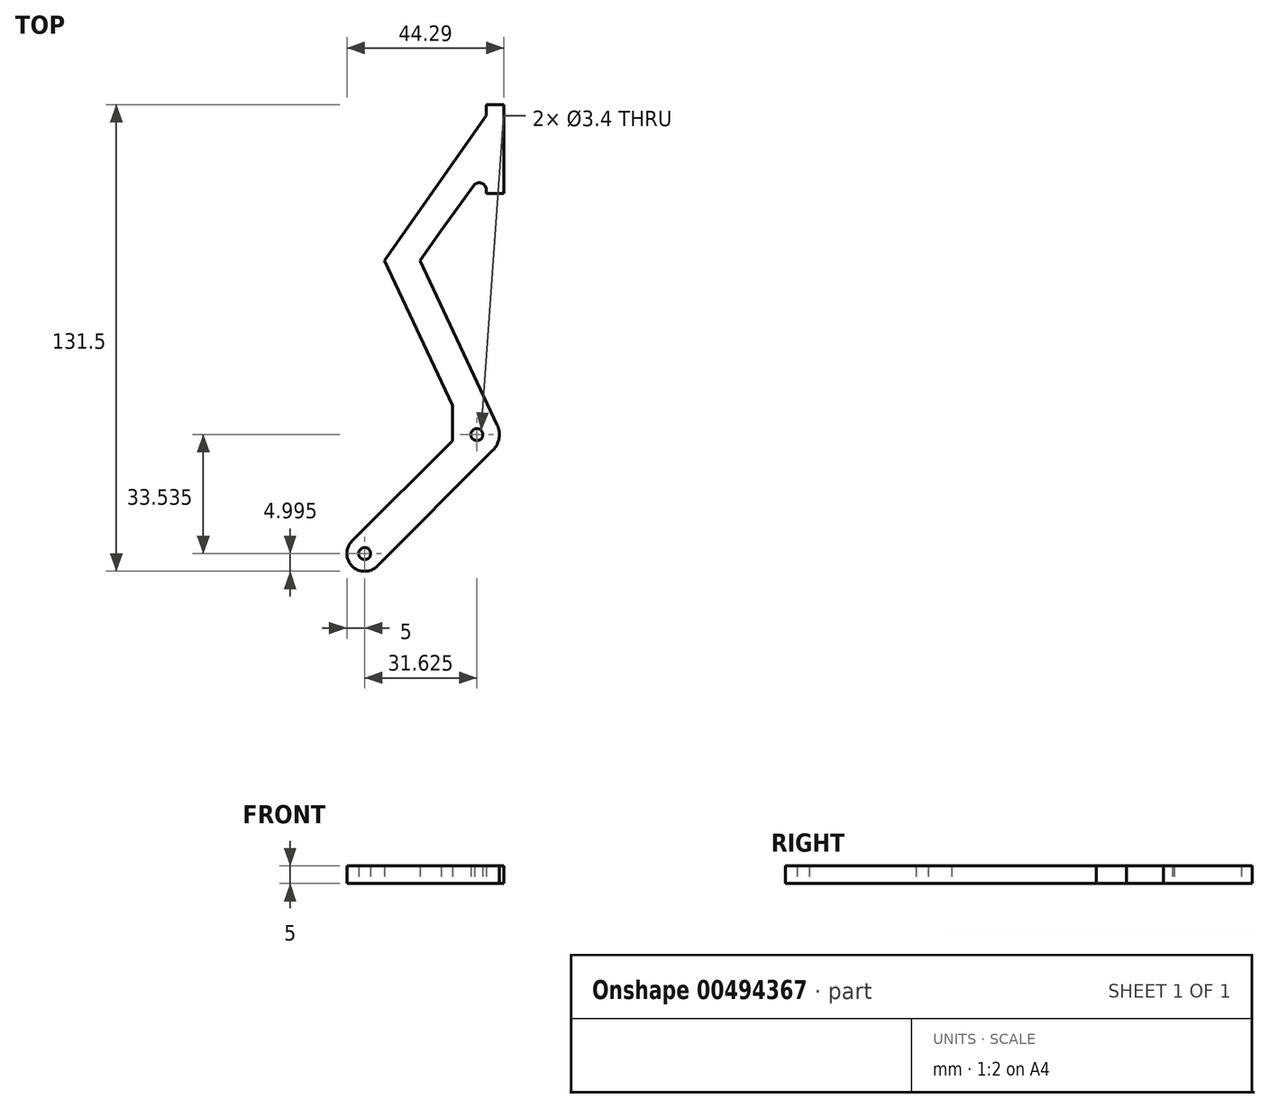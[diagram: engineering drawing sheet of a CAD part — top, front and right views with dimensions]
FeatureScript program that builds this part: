
annotation { "Feature Type Name" : "Feature", "Feature Type Description" : "" }
export const myFeature = defineFeature(function(context is Context, id is Id, definition is map)
    precondition{}
    {
        {
            var Q0;
            Q0=qCreatedBy(makeId("Top.planeOp"),FACE);
            var sketch = newSketch(context, id + "F0", { "sketchPlane" : qUnion([Q0])});
            skLineSegment(sketch, "E0", {"start": v(28.64, 109.53) * mm, "end": v(33.64, 109.53) * mm});
            skLineSegment(sketch, "E1", {"start": v(33.64, 109.53) * mm, "end": v(33.64, 84.53) * mm});
            skLineSegment(sketch, "E2", {"start": v(33.64, 84.53) * mm, "end": v(28.64, 84.53) * mm});
            skLineSegment(sketch, "E3", {"start": v(28.64, 109.53) * mm, "end": v(28.64, 106.53) * mm});
            skLineSegment(sketch, "E4", {"start": v(28.64, 84.53) * mm, "end": v(28.64, 85.53) * mm});
            skLineSegment(sketch, "E5", {"start": v(28.64, 106.53) * mm, "end": v(-0.04, 65.57) * mm});
            skLineSegment(sketch, "E6", {"start": v(-0.04, 65.57) * mm, "end": v(19.1, 24.85) * mm});
            skLineSegment(sketch, "E7", {"start": v(9.96, 65.57) * mm, "end": v(31.72, 19.26) * mm});
            skLineSegment(sketch, "E8", {"start": v(19.1, 24.85) * mm, "end": v(19.1, 14.85) * mm});
            skLineSegment(sketch, "E9", {"start": v(19.1, 14.85) * mm, "end": v(-9.19, -13.44) * mm});
            skLineSegment(sketch, "E10", {"start": v(9.96, 65.57) * mm, "end": v(15.97, 74.15) * mm});
            skArc(sketch, "E11", {"start": v(28.64, 85.53) * mm, "mid": v(27.47, 87.35) * mm, "end": v(25.33, 87.04) * mm});
            skLineSegment(sketch, "E12", {"start": v(15.97, 74.15) * mm, "end": v(25.33, 87.04) * mm});
            skLineSegment(sketch, "E13", {"start": v(19.1, 14.85) * mm, "end": v(26.17, 7.77) * mm});
            skLineSegment(sketch, "E14", {"start": v(26.17, 7.77) * mm, "end": v(30.47, 12.07) * mm});
            skPoint(sketch, "E15.newPointA", {"position": v(35.48, 11.27) * mm});
            skArc(sketch, "E15.filletArc", {"start": v(30.47, 12.07) * mm, "mid": v(32.23, 15.47) * mm, "end": v(31.72, 19.26) * mm});
            skCircle(sketch, "E16", {"center": v(25.98, 16.56) * mm, "radius": 1.7 * mm});
            skLineSegment(sketch, "E17", {"start": v(26.17, 7.77) * mm, "end": v(-2.11, -20.51) * mm});
            skLineSegment(sketch, "E18", {"start": v(-2.11, -20.51) * mm, "end": v(-9.19, -13.44) * mm});
            skArc(sketch, "E19", {"start": v(-9.19, -13.44) * mm, "mid": v(-9.19, -20.51) * mm, "end": v(-2.11, -20.51) * mm});
            skCircle(sketch, "E20", {"center": v(-5.65, -16.97) * mm, "radius": 1.7 * mm});
            skSolve(sketch);
        }
        {
            var Q0;
            Q0 = qSketchRegion(id + "F0", true);
            extrude(context, id + "F1", {"entities" : qUnion([Q0]), "depth" : 5 * mm});
        }
    });
